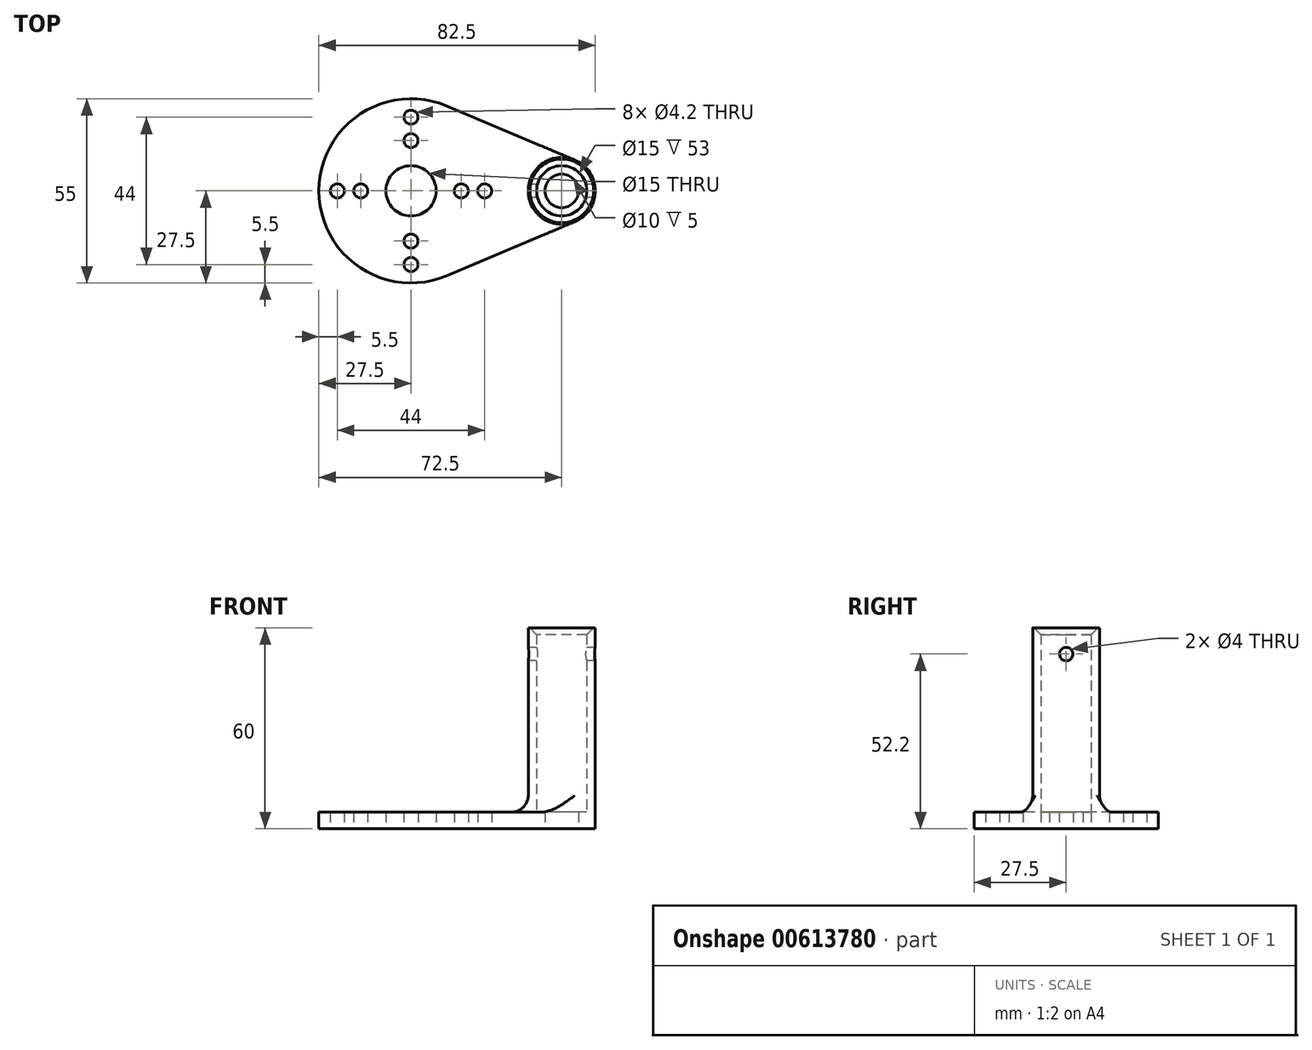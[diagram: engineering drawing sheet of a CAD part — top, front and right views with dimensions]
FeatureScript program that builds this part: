
annotation { "Feature Type Name" : "Feature", "Feature Type Description" : "" }
export const myFeature = defineFeature(function(context is Context, id is Id, definition is map)
    precondition{}
    {
        {
            var Q0;
            Q0=qCreatedBy(makeId("Top.planeOp"),FACE);
            var sketch = newSketch(context, id + "F0", { "sketchPlane" : qUnion([Q0])});
            skCircle(sketch, "E0", {"center": v(0, 0) * mm, "radius": 27.5 * mm});
            skCircle(sketch, "E1", {"center": v(45, 0) * mm, "radius": 10 * mm});
            skLineSegment(sketch, "E2", {"start": v(48.89, 9.21) * mm, "end": v(10.7, 25.34) * mm});
            skCircle(sketch, "E3", {"center": v(0, 22) * mm, "radius": 2.1 * mm});
            skLineSegment(sketch, "E4", {"start": v(-25, -11.46) * mm, "end": v(-25, -11.46) * mm});
            skLineSegment(sketch, "E5.MirrorCS", {"start": v(48.89, -9.21) * mm, "end": v(10.7, -25.34) * mm});
            skCircle(sketch, "E6", {"center": v(0, 15) * mm, "radius": 2.1 * mm});
            skCircle(sketch, "E7.1.0", {"center": v(-22, 0) * mm, "radius": 2.1 * mm});
            skCircle(sketch, "E7.1.1", {"center": v(-15, 0) * mm, "radius": 2.1 * mm});
            skCircle(sketch, "E7.2.0", {"center": v(0, -22) * mm, "radius": 2.1 * mm});
            skCircle(sketch, "E7.2.1", {"center": v(0, -15) * mm, "radius": 2.1 * mm});
            skCircle(sketch, "E7.3.0", {"center": v(22, 0) * mm, "radius": 2.1 * mm});
            skCircle(sketch, "E7.3.1", {"center": v(15, 0) * mm, "radius": 2.1 * mm});
            skCircle(sketch, "E8", {"center": v(45, 0) * mm, "radius": 7.5 * mm});
            skCircle(sketch, "E9", {"center": v(45, 0) * mm, "radius": 5 * mm});
            skCircle(sketch, "E10", {"center": v(0, 0) * mm, "radius": 7.5 * mm});
            skSolve(sketch);
        }
        {
            var Q0;
            Q0=makeQuery(id+"F0.imprint","IMPRINT",FACE,{"disambiguationData":[TD([[makeQuery(id+"F0.imprint","IMPRINT",EDGE,{"derivedFrom":sQuery(id+"F0.wireOp",EDGE,"E3")}),-1.0]])]});
            var Q1;
            {var subQ0=sQuery(id+"F0.wireOp",EDGE,"E2");Q1=makeQuery(id+"F0.imprint","IMPRINT",FACE,{"disambiguationData":[TD([[makeQuery(id+"F0.imprint","IMPRINT",EDGE,{"derivedFrom":subQ0}),1.0]])]});}
            var Q2;
            Q2=makeQuery(id+"F0.imprint","IMPRINT",FACE,{"disambiguationData":[TD([[makeQuery(id+"F0.imprint","IMPRINT",EDGE,{"derivedFrom":sQuery(id+"F0.wireOp",EDGE,"E8")}),-1.0]])]});
            var Q3;
            Q3=makeQuery(id+"F0.imprint","IMPRINT",FACE,{"disambiguationData":[TD([[makeQuery(id+"F0.imprint","IMPRINT",EDGE,{"derivedFrom":sQuery(id+"F0.wireOp",EDGE,"E8")}),1.0]])]});
            extrude(context, id + "F1", {"entities" : qUnion([Q0, Q1, Q2, Q3]), "depth" : 5 * mm, "offsetDistance" : 25 * mm});
        }
        {
            var Q0;
            Q0=makeQuery(id+"F0.imprint","IMPRINT",FACE,{"disambiguationData":[TD([[makeQuery(id+"F0.imprint","IMPRINT",EDGE,{"derivedFrom":sQuery(id+"F0.wireOp",EDGE,"E8")}),-1.0]])]});
            var Q1;
            Q1=sQuery(id+"F0.wireOp",EDGE,"E8");
            var Q2;
            Q2=sQuery(id+"F0.wireOp",EDGE,"E1");
            extrude(context, id + "F2", {"entities" : qUnion([Q0]), "operationType" : NewBodyOperationType.ADD, "surfaceEntities" : qUnion([Q1, Q2]), "depth" : 60 * mm, "offsetDistance" : 25 * mm});
        }
        {
            var Q0;
            {var subQ0=sQuery(id+"F0.wireOp",EDGE,"E1");Q0=makeQuery(id+"F2.boolean.opBoolean","INTERSECT",EDGE,{"derivedFrom":[makeQuery(id+"F1.opExtrude","CAP_FACE",FACE,{"disambiguationData":[OSD([sQuery(id+"F0.wireOp",EDGE,"E0"),subQ0,sQuery(id+"F0.wireOp",EDGE,"E2"),sQuery(id+"F0.wireOp",EDGE,"E3"),sQuery(id+"F0.wireOp",EDGE,"E5.MirrorCS"),sQuery(id+"F0.wireOp",EDGE,"E6"),sQuery(id+"F0.wireOp",EDGE,"E7.1.0"),sQuery(id+"F0.wireOp",EDGE,"E7.1.1"),sQuery(id+"F0.wireOp",EDGE,"E7.2.0"),sQuery(id+"F0.wireOp",EDGE,"E7.2.1"),sQuery(id+"F0.wireOp",EDGE,"E7.3.0"),sQuery(id+"F0.wireOp",EDGE,"E7.3.1"),sQuery(id+"F0.wireOp",EDGE,"E9")])],"isStart":false}),makeQuery(id+"F2.opExtrude","SWEPT_FACE",FACE,{"disambiguationData":[OSD([subQ0])]})]});}
            fillet(context, id + "F3", {"entities" : qUnion([Q0]), "radius" : 5 * mm, "tangentPropagation" : true, "allowEdgeOverflow" : false});
        }
        {
            var Q0;
            Q0=qCreatedBy(makeId("Right.planeOp"),FACE);
            var sketch = newSketch(context, id + "F4", { "sketchPlane" : qUnion([Q0])});
            skLineSegment(sketch, "E11.0", {"start": v(-5, 5) * mm, "end": v(5, 5) * mm});
            skLineSegment(sketch, "E12.0", {"start": v(-7.5, 60) * mm, "end": v(7.5, 60) * mm});
            skLineSegment(sketch, "E13", {"start": v(5, 50.2) * mm, "end": v(-5, 50.2) * mm, "construction": true});
            skCircle(sketch, "E14", {"center": v(0, 52.2) * mm, "radius": 2 * mm});
            skPoint(sketch, "E14.centerSnap0", {"position": v(0, 50.2) * mm});
            skSolve(sketch);
        }
        {
            var Q0;
            Q0 = qSketchRegion(id + "F4", true);
            extrude(context, id + "F5", {"entities" : qUnion([Q0]), "operationType" : NewBodyOperationType.REMOVE, "endBound" : BoundingType.THROUGH_ALL, "depth" : 25 * mm, "offsetDistance" : 25 * mm});
        }
        {
            var Q0;
            Q0=makeQuery(id+"F2.opExtrude","CAP_EDGE",EDGE,{"disambiguationData":[OSD([sQuery(id+"F0.wireOp",EDGE,"E8")])],"isStart":false});
            chamfer(context, id + "F6", {"entities" : qUnion([Q0]), "width" : 2 * mm, "tangentPropagation" : true});
        }
    });
